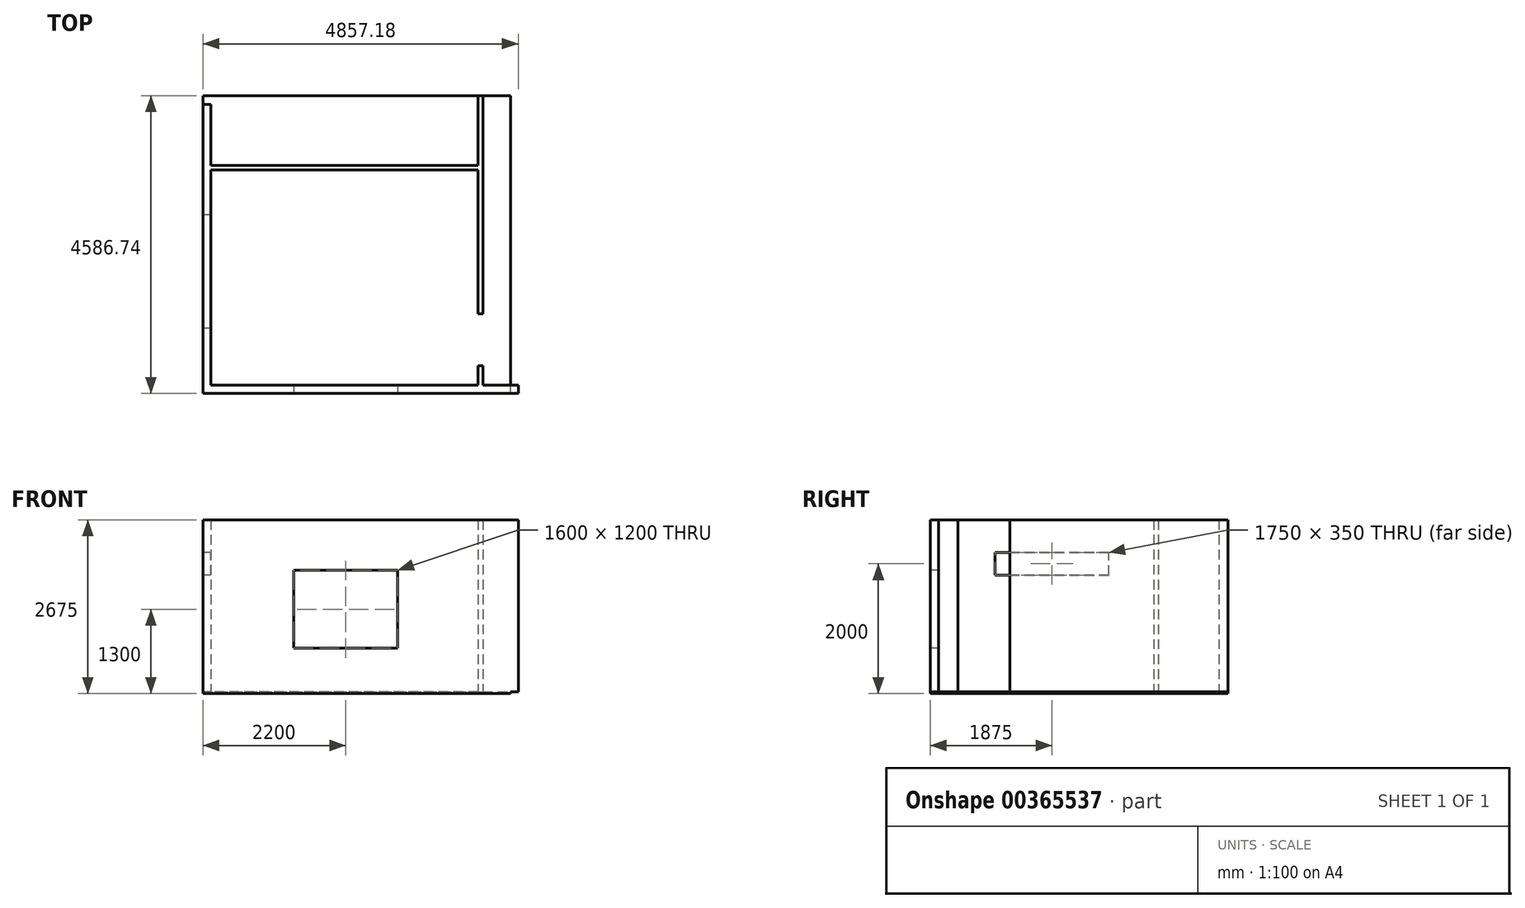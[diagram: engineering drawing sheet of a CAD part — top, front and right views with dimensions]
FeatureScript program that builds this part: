
annotation { "Feature Type Name" : "Feature", "Feature Type Description" : "" }
export const myFeature = defineFeature(function(context is Context, id is Id, definition is map)
    precondition{}
    {
        {
            var Q0;
            Q0=qCreatedBy(makeId("Top.planeOp"),FACE);
            var sketch = newSketch(context, id + "F0", { "sketchPlane" : qUnion([Q0])});
            skLineSegment(sketch, "E0.bottom", {"start": v(2056, -1657) * mm, "end": v(-2056, -1657) * mm});
            skLineSegment(sketch, "E0.top", {"start": v(2056, 1657) * mm, "end": v(-2056, 1657) * mm});
            skLineSegment(sketch, "E0.left", {"start": v(2056, -1657) * mm, "end": v(2056, -1357) * mm});
            skLineSegment(sketch, "E0.right", {"start": v(-2056, -1657) * mm, "end": v(-2056, 1657) * mm});
            skPoint(sketch, "E0.middle", {"position": v(0, 0) * mm});
            skLineSegment(sketch, "E1.top", {"start": v(-2056, 2665.97) * mm, "end": v(-2181, 2665.97) * mm});
            skLineSegment(sketch, "E1.right", {"start": v(-2181, -1657) * mm, "end": v(-2181, 2665.97) * mm});
            skLineSegment(sketch, "E2.bottom", {"start": v(-2056, -1657) * mm, "end": v(2056, -1657) * mm});
            skLineSegment(sketch, "E2.top", {"start": v(-2181, -1782) * mm, "end": v(2676.18, -1782) * mm});
            skLineSegment(sketch, "E2.left", {"start": v(-2181, -1657) * mm, "end": v(-2181, -1782) * mm});
            skLineSegment(sketch, "E2.right", {"start": v(2676.18, -1657) * mm, "end": v(2676.18, -1782) * mm});
            skLineSegment(sketch, "E3.top", {"start": v(2056, -1357) * mm, "end": v(2131, -1357) * mm});
            skLineSegment(sketch, "E3.right", {"start": v(2131, -1657) * mm, "end": v(2131, -1357) * mm});
            skLineSegment(sketch, "E4.bottom", {"start": v(2056, -557) * mm, "end": v(2131, -557) * mm});
            skLineSegment(sketch, "E4.top", {"start": v(2056, 2804.74) * mm, "end": v(2131, 2804.74) * mm});
            skLineSegment(sketch, "E4.left", {"start": v(2056, -557) * mm, "end": v(2056, 1657) * mm});
            skLineSegment(sketch, "E4.right", {"start": v(2131, -557) * mm, "end": v(2131, 2804.74) * mm});
            skLineSegment(sketch, "E5.bottom", {"start": v(-2056, 1657) * mm, "end": v(2056, 1657) * mm});
            skLineSegment(sketch, "E5.top", {"start": v(-2056, 1732) * mm, "end": v(2056, 1732) * mm});
            skLineSegment(sketch, "E6.trimOffspring", {"start": v(2131, -1657) * mm, "end": v(2676.18, -1657) * mm});
            skLineSegment(sketch, "E7.trimOffspring", {"start": v(-2056, 1732) * mm, "end": v(-2056, 2665.97) * mm});
            skLineSegment(sketch, "E8.trimOffspring", {"start": v(2056, 1732) * mm, "end": v(2056, 2804.74) * mm});
            skSolve(sketch);
        }
        {
            var Q0;
            Q0 = qSketchRegion(id + "F0", true);
            extrude(context, id + "F1", {"entities" : qUnion([Q0]), "depth" : 2650 * mm});
        }
        {
            var Q0;
            Q0=makeQuery(id+"F1.opExtrude","CAP_FACE",FACE,{"disambiguationData":[OSD([sQuery(id+"F0.wireOp",EDGE,"E1.top"),sQuery(id+"F0.wireOp",EDGE,"E0.right"),sQuery(id+"F0.wireOp",EDGE,"E1.right"),sQuery(id+"F0.wireOp",EDGE,"E2.bottom"),sQuery(id+"F0.wireOp",EDGE,"E2.top"),sQuery(id+"F0.wireOp",EDGE,"E2.left"),sQuery(id+"F0.wireOp",EDGE,"E2.right"),sQuery(id+"F0.wireOp",EDGE,"E3.top"),sQuery(id+"F0.wireOp",EDGE,"E0.left"),sQuery(id+"F0.wireOp",EDGE,"E3.right"),sQuery(id+"F0.wireOp",EDGE,"E4.bottom"),sQuery(id+"F0.wireOp",EDGE,"E4.top"),sQuery(id+"F0.wireOp",EDGE,"E4.right"),sQuery(id+"F0.wireOp",EDGE,"E5.bottom"),sQuery(id+"F0.wireOp",EDGE,"E5.top"),sQuery(id+"F0.wireOp",EDGE,"E6.trimOffspring"),sQuery(id+"F0.wireOp",EDGE,"E7.trimOffspring"),sQuery(id+"F0.wireOp",EDGE,"E8.trimOffspring"),sQuery(id+"F0.wireOp",EDGE,"E4.left")])],"isStart":true});
            var sketch = newSketch(context, id + "F2", { "sketchPlane" : qUnion([Q0])});
            skLineSegment(sketch, "E9.bottom", {"start": v(-2181, 1782) * mm, "end": v(2555.85, 1782) * mm});
            skLineSegment(sketch, "E9.top", {"start": v(-2181, -2804.74) * mm, "end": v(2555.85, -2804.74) * mm});
            skLineSegment(sketch, "E9.left", {"start": v(-2181, 1782) * mm, "end": v(-2181, -2804.74) * mm});
            skLineSegment(sketch, "E9.right", {"start": v(2555.85, 1782) * mm, "end": v(2555.85, -2804.74) * mm});
            skSolve(sketch);
        }
        {
            var Q0;
            Q0 = qSketchRegion(id + "F2", true);
            extrude(context, id + "F3", {"entities" : qUnion([Q0]), "operationType" : NewBodyOperationType.ADD, "depth" : 25 * mm});
        }
        {
            var Q0;
            Q0=makeQuery(id+"F3.boolean.opBoolean","MERGE",FACE,{"derivedFrom":[makeQuery(id+"F1.opExtrude","SWEPT_FACE",FACE,{"disambiguationData":[OSD([sQuery(id+"F0.wireOp",EDGE,"E2.top")])]}),makeQuery(id+"F3.opExtrude","SWEPT_FACE",FACE,{"disambiguationData":[OSD([sQuery(id+"F2.wireOp",EDGE,"E9.bottom")])]})]});
            var sketch = newSketch(context, id + "F4", { "sketchPlane" : qUnion([Q0])});
            skLineSegment(sketch, "E10.bottom", {"start": v(-781, 1875) * mm, "end": v(819, 1875) * mm});
            skLineSegment(sketch, "E10.top", {"start": v(-781, 675) * mm, "end": v(819, 675) * mm});
            skLineSegment(sketch, "E10.left", {"start": v(-781, 1875) * mm, "end": v(-781, 675) * mm});
            skLineSegment(sketch, "E10.right", {"start": v(819, 1875) * mm, "end": v(819, 675) * mm});
            skSolve(sketch);
        }
        {
            var Q0;
            Q0 = qSketchRegion(id + "F4", true);
            extrude(context, id + "F5", {"entities" : qUnion([Q0]), "operationType" : NewBodyOperationType.REMOVE, "endBound" : BoundingType.UP_TO_NEXT, "oppositeDirection" : true, "depth" : 25 * mm});
        }
        {
            var Q0;
            Q0=makeQuery(id+"F3.boolean.opBoolean","MERGE",FACE,{"derivedFrom":[makeQuery(id+"F1.opExtrude","SWEPT_FACE",FACE,{"disambiguationData":[OSD([sQuery(id+"F0.wireOp",EDGE,"E1.right"),sQuery(id+"F0.wireOp",EDGE,"E2.left")])]}),makeQuery(id+"F3.opExtrude","SWEPT_FACE",FACE,{"disambiguationData":[OSD([sQuery(id+"F2.wireOp",EDGE,"E9.left")])]})]});
            var sketch = newSketch(context, id + "F6", { "sketchPlane" : qUnion([Q0])});
            skLineSegment(sketch, "E11.bottom", {"start": v(-968, 2150) * mm, "end": v(782, 2150) * mm});
            skLineSegment(sketch, "E11.top", {"start": v(-968, 1800) * mm, "end": v(782, 1800) * mm});
            skLineSegment(sketch, "E11.left", {"start": v(-968, 2150) * mm, "end": v(-968, 1800) * mm});
            skLineSegment(sketch, "E11.right", {"start": v(782, 2150) * mm, "end": v(782, 1800) * mm});
            skSolve(sketch);
        }
        {
            var Q0;
            Q0 = qSketchRegion(id + "F6", true);
            extrude(context, id + "F7", {"entities" : qUnion([Q0]), "operationType" : NewBodyOperationType.REMOVE, "endBound" : BoundingType.UP_TO_NEXT, "oppositeDirection" : true, "depth" : 25 * mm});
        }
    });
